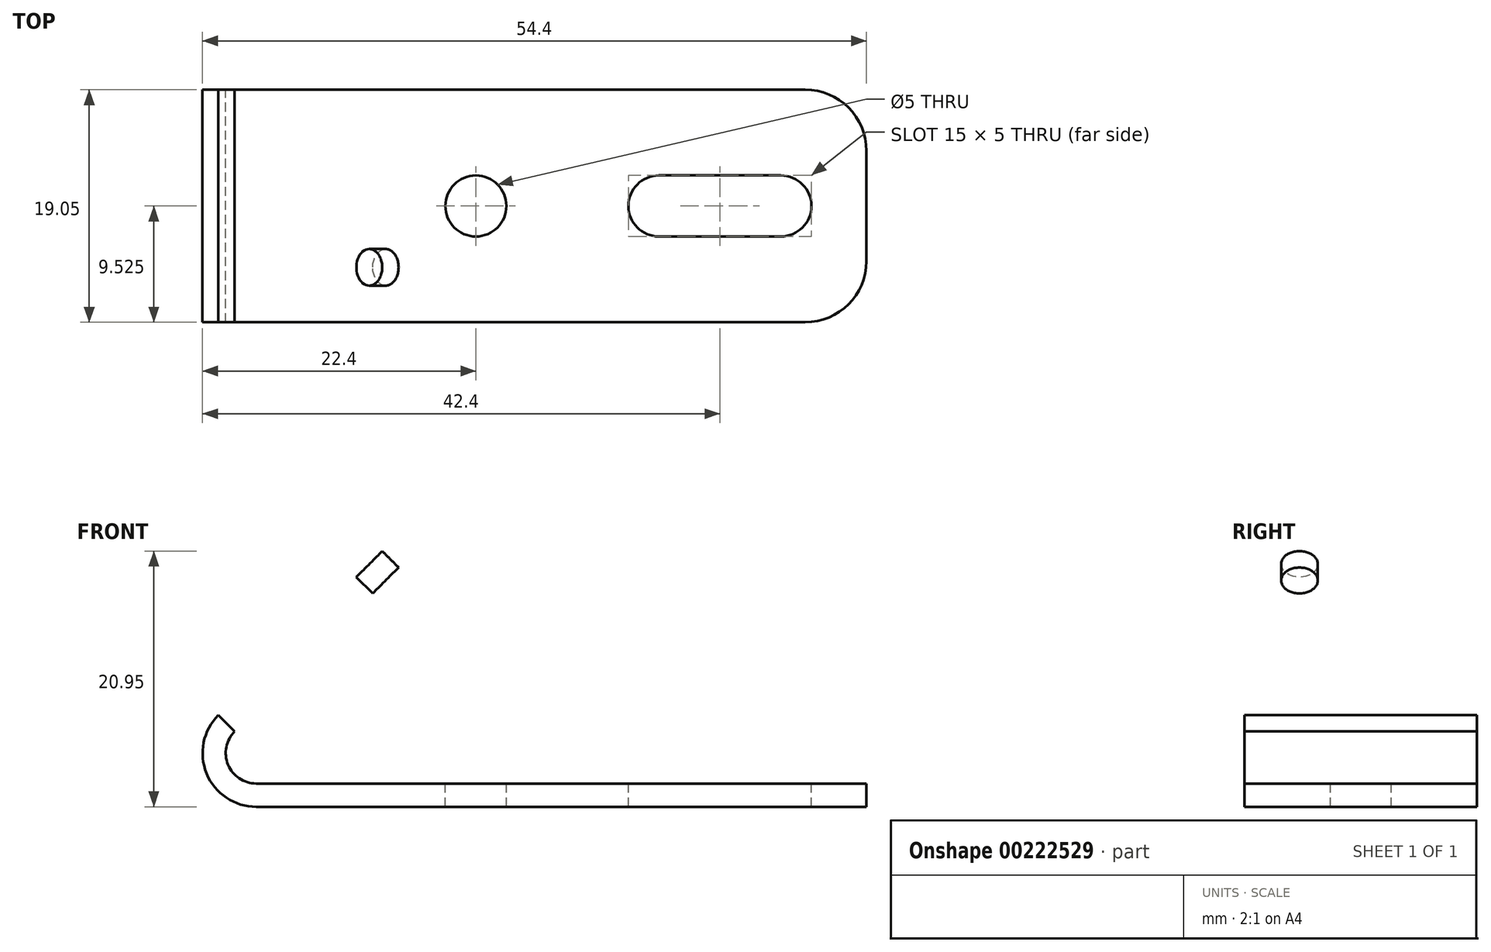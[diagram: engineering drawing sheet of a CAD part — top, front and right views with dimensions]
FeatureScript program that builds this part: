
annotation { "Feature Type Name" : "Feature", "Feature Type Description" : "" }
export const myFeature = defineFeature(function(context is Context, id is Id, definition is map)
    precondition{}
    {
        {
            var Q0;
            Q0=qCreatedBy(makeId("Front.planeOp"),FACE);
            var sketch = newSketch(context, id + "F0", { "sketchPlane" : qUnion([Q0])});
            skLineSegment(sketch, "E0", {"start": v(0, 0) * mm, "end": v(-50, 0) * mm});
            skLineSegment(sketch, "E1", {"start": v(-53.11, 7.51) * mm, "end": v(-35.43, 25.19) * mm});
            skLineSegment(sketch, "E2", {"start": v(-35.43, 25.19) * mm, "end": v(-34.1, 23.85) * mm});
            skLineSegment(sketch, "E3", {"start": v(-34.1, 23.85) * mm, "end": v(-51.77, 6.17) * mm});
            skLineSegment(sketch, "E4", {"start": v(-50, 1.9) * mm, "end": v(0, 1.9) * mm});
            skLineSegment(sketch, "E5", {"start": v(0, 1.9) * mm, "end": v(0, 0) * mm});
            skPoint(sketch, "E6.visualSharp", {"position": v(-56.04, 1.9) * mm});
            skPoint(sketch, "E7.visualSharp", {"position": v(-60.62, 0) * mm});
            skArc(sketch, "E7.filletArc", {"start": v(-53.11, 7.51) * mm, "mid": v(-54.07, 2.72) * mm, "end": v(-50, 0) * mm});
            skArc(sketch, "E8.filletArc", {"start": v(-51.77, 6.17) * mm, "mid": v(-52.3, 3.44) * mm, "end": v(-50, 1.9) * mm});
            skSolve(sketch);
        }
        {
            var Q0;
            Q0 = qSketchRegion(id + "F0", true);
            extrude(context, id + "F1", {"entities" : qUnion([Q0]), "depth" : 19.05 * mm});
        }
        {
            var Q0;
            Q0=makeQuery(id+"F1.opExtrude","SWEPT_FACE",FACE,{"disambiguationData":[OSD([sQuery(id+"F0.wireOp",EDGE,"E4")])]});
            var sketch = newSketch(context, id + "F2", { "sketchPlane" : qUnion([Q0])});
            skArc(sketch, "E9", {"start": v(-7, -12.03) * mm, "mid": v(-4.5, -9.53) * mm, "end": v(-7, -7.03) * mm});
            skPoint(sketch, "E9.centerSnap0", {"position": v(0, -9.53) * mm});
            skArc(sketch, "E10", {"start": v(-17, -7.03) * mm, "mid": v(-19.5, -9.53) * mm, "end": v(-17, -12.03) * mm});
            skLineSegment(sketch, "E11", {"start": v(-7, -7.03) * mm, "end": v(-17, -7.03) * mm});
            skLineSegment(sketch, "E12", {"start": v(-7, -12.03) * mm, "end": v(-17, -12.03) * mm});
            skCircle(sketch, "E13", {"center": v(-32, -9.53) * mm, "radius": 2.5 * mm});
            skPoint(sketch, "E13.centerSnap0", {"position": v(-19.5, -9.53) * mm});
            skSolve(sketch);
        }
        {
            var Q0;
            Q0=makeQuery(id+"F2.imprint","IMPRINT",FACE,{"disambiguationData":[TD([[makeQuery(id+"F2.imprint","IMPRINT",EDGE,{"derivedFrom":sQuery(id+"F2.wireOp",EDGE,"E13")}),1.0]])]});
            var Q1;
            Q1=makeQuery(id+"F2.imprint","IMPRINT",FACE,{"disambiguationData":[TD([[makeQuery(id+"F2.imprint","IMPRINT",EDGE,{"derivedFrom":sQuery(id+"F2.wireOp",EDGE,"E9")}),1.0]])]});
            extrude(context, id + "F3", {"entities" : qUnion([Q0, Q1]), "operationType" : NewBodyOperationType.REMOVE, "endBound" : BoundingType.UP_TO_NEXT, "oppositeDirection" : true, "depth" : 25 * mm});
        }
        {
            var Q0;
            Q0=makeQuery(id+"F1.opExtrude","SWEPT_FACE",FACE,{"disambiguationData":[OSD([sQuery(id+"F0.wireOp",EDGE,"E1")])]});
            var sketch = newSketch(context, id + "F4", { "sketchPlane" : qUnion([Q0])});
            skCircle(sketch, "E14", {"center": v(4.5, -14.74) * mm, "radius": 1.5 * mm});
            skLineSegment(sketch, "E15", {"start": v(9.53, -32.24) * mm, "end": v(9.53, -7.24) * mm, "construction": true});
            skCircle(sketch, "E16.MirrorC", {"center": v(14.55, -14.74) * mm, "radius": 1.5 * mm});
            skSolve(sketch);
        }
        {
            var Q0;
            Q0=makeQuery(id+"F4.imprint","IMPRINT",FACE,{"disambiguationData":[TD([[makeQuery(id+"F4.imprint","IMPRINT",EDGE,{"derivedFrom":sQuery(id+"F4.wireOp",EDGE,"E16.MirrorC")}),-1.0]])]});
            var Q1;
            Q1=makeQuery(id+"F4.imprint","IMPRINT",FACE,{"disambiguationData":[TD([[makeQuery(id+"F4.imprint","IMPRINT",EDGE,{"derivedFrom":sQuery(id+"F4.wireOp",EDGE,"E14")}),1.0]])]});
            extrude(context, id + "F5", {"entities" : qUnion([Q0, Q1]), "operationType" : NewBodyOperationType.REMOVE, "endBound" : BoundingType.UP_TO_NEXT, "oppositeDirection" : true, "depth" : 25 * mm});
        }
        {
            var Q0;
            Q0=makeQuery(id+"F1.opExtrude","CAP_EDGE",EDGE,{"disambiguationData":[OSD([sQuery(id+"F0.wireOp",EDGE,"E2")])],"isStart":true});
            var Q1;
            Q1=makeQuery(id+"F1.opExtrude","CAP_EDGE",EDGE,{"disambiguationData":[OSD([sQuery(id+"F0.wireOp",EDGE,"E2")])],"isStart":false});
            var Q2;
            Q2=makeQuery(id+"F1.opExtrude","CAP_EDGE",EDGE,{"disambiguationData":[OSD([sQuery(id+"F0.wireOp",EDGE,"E5")])],"isStart":true});
            var Q3;
            Q3=makeQuery(id+"F1.opExtrude","CAP_EDGE",EDGE,{"disambiguationData":[OSD([sQuery(id+"F0.wireOp",EDGE,"E5")])],"isStart":false});
            fillet(context, id + "F6", {"entities" : qUnion([Q0, Q1, Q2, Q3]), "radius" : 5 * mm, "tangentPropagation" : true, "allowEdgeOverflow" : false});
        }
    });
